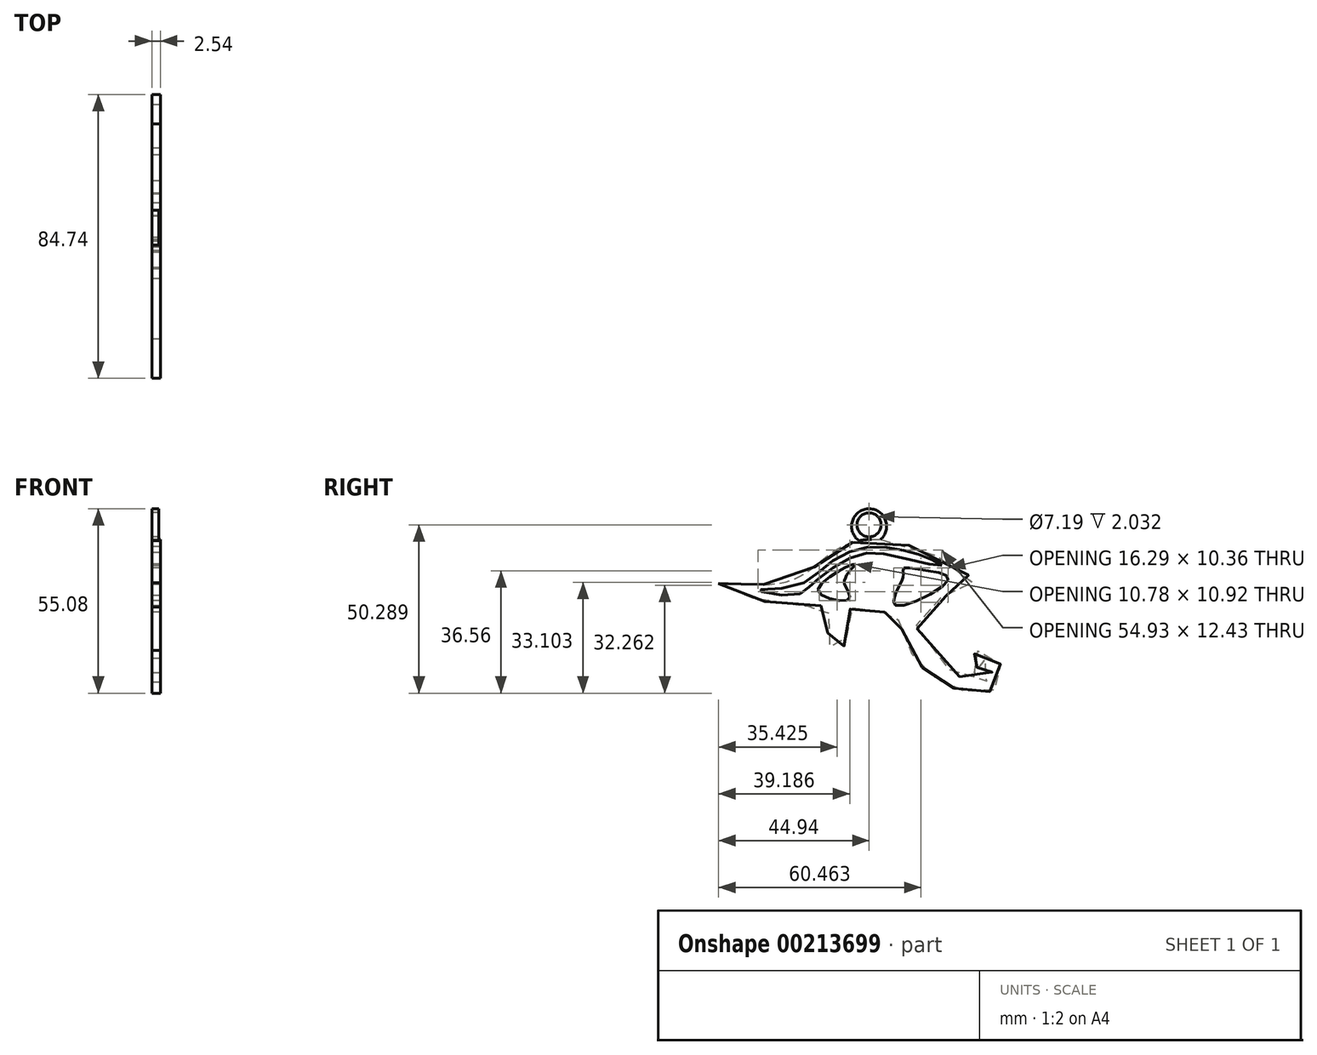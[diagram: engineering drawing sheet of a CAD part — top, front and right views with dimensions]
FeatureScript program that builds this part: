
annotation { "Feature Type Name" : "Feature", "Feature Type Description" : "" }
export const myFeature = defineFeature(function(context is Context, id is Id, definition is map)
    precondition{}
    {
        {
            var Q0;
            Q0=qCreatedBy(makeId("Right.planeOp"),FACE);
            var sketch = newSketch(context, id + "F0", { "sketchPlane" : qUnion([Q0])});
            skFitSpline(sketch, "E0", {"points": [v(-62.31, 39.84) * mm, v(-43.64, 40.06) * mm, v(-27.8, 49.61) * mm, v(-7.82, 52) * mm, v(13.46, 39.4) * mm, v(-2.82, 31.6) * mm, v(11.07, 11.4) * mm, v(19.32, 12.92) * mm, v(16.28, 17.48) * mm, v(14.11, 13.14) * mm, v(14.11, 19) * mm, v(20.4, 18.13) * mm, v(21.5, 9.44) * mm, v(13.24, 7.27) * mm, v(3.47, 10.96) * mm, v(-5.21, 20.08) * mm, v(-9.77, 30.94) * mm, v(-13.9, 31.37) * mm, v(-23.23, 32.03) * mm, v(-24.97, 20.95) * mm, v(-29.1, 21.17) * mm, v(-29.53, 32.24) * mm, v(-39.08, 32.9) * mm, v(-62.31, 39.84) * mm]});
            skSolve(sketch);
        }
        {
            var Q0;
            Q0=makeQuery(id+"F0.imprint","IMPRINT",FACE,{"disambiguationData":[TD([[makeQuery(id+"F0.imprint","IMPRINT",EDGE,{"derivedFrom":sQuery(id+"F0.wireOp",EDGE,"E0")}),-1.0]])]});
            extrude(context, id + "F1", {"entities" : qUnion([Q0]), "depth" : 2.54 * mm});
        }
        {
            var Q0;
            Q0=makeQuery(id+"F1.opExtrude","CAP_FACE",FACE,{"disambiguationData":[OSD([sQuery(id+"F0.wireOp",EDGE,"E0")])],"isStart":false});
            var sketch = newSketch(context, id + "F2", { "sketchPlane" : qUnion([Q0])});
            skFitSpline(sketch, "E1", {"points": [v(4.34, 45.27) * mm, v(0, 47.66) * mm, v(-7.38, 49.83) * mm, v(-18.46, 50.7) * mm, v(-29.53, 45.7) * mm, v(-39.3, 39.2) * mm, v(-50.59, 37.89) * mm, v(-40.17, 36.37) * mm, v(-35.4, 38.76) * mm, v(-29.96, 43.32) * mm, v(-19.54, 48.74) * mm, v(-8.03, 47.66) * mm, v(4.34, 45.27) * mm]});
            skSolve(sketch);
        }
        {
            var Q0;
            Q0 = qSketchRegion(id + "F2", true);
            extrude(context, id + "F3", {"entities" : qUnion([Q0]), "operationType" : NewBodyOperationType.REMOVE, "oppositeDirection" : true, "depth" : 25.4 * mm});
        }
        {
            var Q0;
            Q0=makeQuery(id+"F1.opExtrude","CAP_FACE",FACE,{"disambiguationData":[OSD([sQuery(id+"F0.wireOp",EDGE,"E0")])],"isStart":false});
            var sketch = newSketch(context, id + "F4", { "sketchPlane" : qUnion([Q0])});
            skFitSpline(sketch, "E2", {"points": [v(6.3, 40.93) * mm, v(0, 43.75) * mm, v(-7.17, 44.4) * mm, v(-7.18, 43.42) * mm, v(-7.17, 41.8) * mm, v(-7.48, 41) * mm, v(-8.12, 39.78) * mm, v(-8.73, 38.56) * mm, v(-9.34, 37.15) * mm, v(-9.93, 35.22) * mm, v(-9.98, 35) * mm, v(-9.34, 33.33) * mm, v(6.3, 40.93) * mm]});
            skFitSpline(sketch, "E3", {"points": [v(-21.5, 45.7) * mm, v(-22.59, 45.5) * mm, v(-23.48, 45.14) * mm, v(-24.53, 44.62) * mm, v(-32.57, 37.67) * mm, v(-23.67, 35.07) * mm, v(-23.47, 37.16) * mm, v(-24.27, 38.9) * mm, v(-24.75, 40.28) * mm, v(-24.44, 41.66) * mm, v(-23.6, 43.06) * mm, v(-21.5, 45.7) * mm]});
            skSolve(sketch);
        }
        {
            var Q0;
            Q0 = qSketchRegion(id + "F4", true);
            extrude(context, id + "F5", {"entities" : qUnion([Q0]), "operationType" : NewBodyOperationType.REMOVE, "oppositeDirection" : true, "depth" : 25.4 * mm});
        }
        {
            var Q0;
            Q0=qCreatedBy(makeId("Right.planeOp"),FACE);
            var sketch = newSketch(context, id + "F6", { "sketchPlane" : qUnion([Q0])});
            skCircle(sketch, "E4", {"center": v(-17.37, 57) * mm, "radius": 5.23 * mm});
            skSolve(sketch);
        }
        {
            var Q0;
            Q0 = qSketchRegion(id + "F6", true);
            extrude(context, id + "F7", {"entities" : qUnion([Q0]), "operationType" : NewBodyOperationType.ADD, "depth" : 2.03 * mm});
        }
        {
            var Q0;
            Q0=qCreatedBy(makeId("Right.planeOp"),FACE);
            var sketch = newSketch(context, id + "F8", { "sketchPlane" : qUnion([Q0])});
            skCircle(sketch, "E5", {"center": v(-17.37, 57.43) * mm, "radius": 3.6 * mm});
            skSolve(sketch);
        }
        {
            var Q0;
            Q0 = qSketchRegion(id + "F8", true);
            extrude(context, id + "F9", {"entities" : qUnion([Q0]), "operationType" : NewBodyOperationType.REMOVE, "depth" : 19.3 * mm});
        }
        {
            var Q0;
            Q0 = qSketchRegion(id + "F4", true);
            extrude(context, id + "F10", {"entities" : qUnion([Q0]), "operationType" : NewBodyOperationType.REMOVE, "oppositeDirection" : true, "depth" : 25.4 * mm});
        }
        {
            var Q0;
            Q0=makeQuery(id+"F1.opExtrude","SWEPT_BODY",BODY,{"disambiguationData":[OSD([sQuery(id+"F0.wireOp",EDGE,"E0")])]});
            transform(context, id + "F11", {"entities" : qUnion([Q0]), "transformType" : TransformType.TRANSLATION_3D, "dx" : 15.5 * mm, "dy" : 32 * mm, "dz" : 0 * mm, "makeCopy" : true});
        }
        {
            var Q0;
            Q0=makeQuery(id+"F11.opPattern","COPY",BODY,{"derivedFrom":makeQuery(id+"F1.opExtrude","SWEPT_BODY",BODY,{"disambiguationData":[OSD([sQuery(id+"F0.wireOp",EDGE,"E0")])]}),"instanceName":"1"});
            var Q1;
            Q1=qCreatedBy(makeId("Top.planeOp"),FACE);
            mirror(context, id + "F12", {"entities" : qUnion([Q0]), "mirrorPlane" : qUnion([Q1])});
        }
        {
            var Q0;
            Q0=makeQuery(id+"F12.opPattern","COPY",BODY,{"derivedFrom":makeQuery(id+"F11.opPattern","COPY",BODY,{"derivedFrom":makeQuery(id+"F1.opExtrude","SWEPT_BODY",BODY,{"disambiguationData":[OSD([sQuery(id+"F0.wireOp",EDGE,"E0")])]}),"instanceName":"1"}),"instanceName":"1"});
            var Q1;
            Q1=makeQuery(id+"F11.opPattern","COPY",BODY,{"derivedFrom":makeQuery(id+"F1.opExtrude","SWEPT_BODY",BODY,{"disambiguationData":[OSD([sQuery(id+"F0.wireOp",EDGE,"E0")])]}),"instanceName":"1"});
            deleteBodies(context, id + "F13", {"entities" : qUnion([Q0, Q1])});
        }
    });
